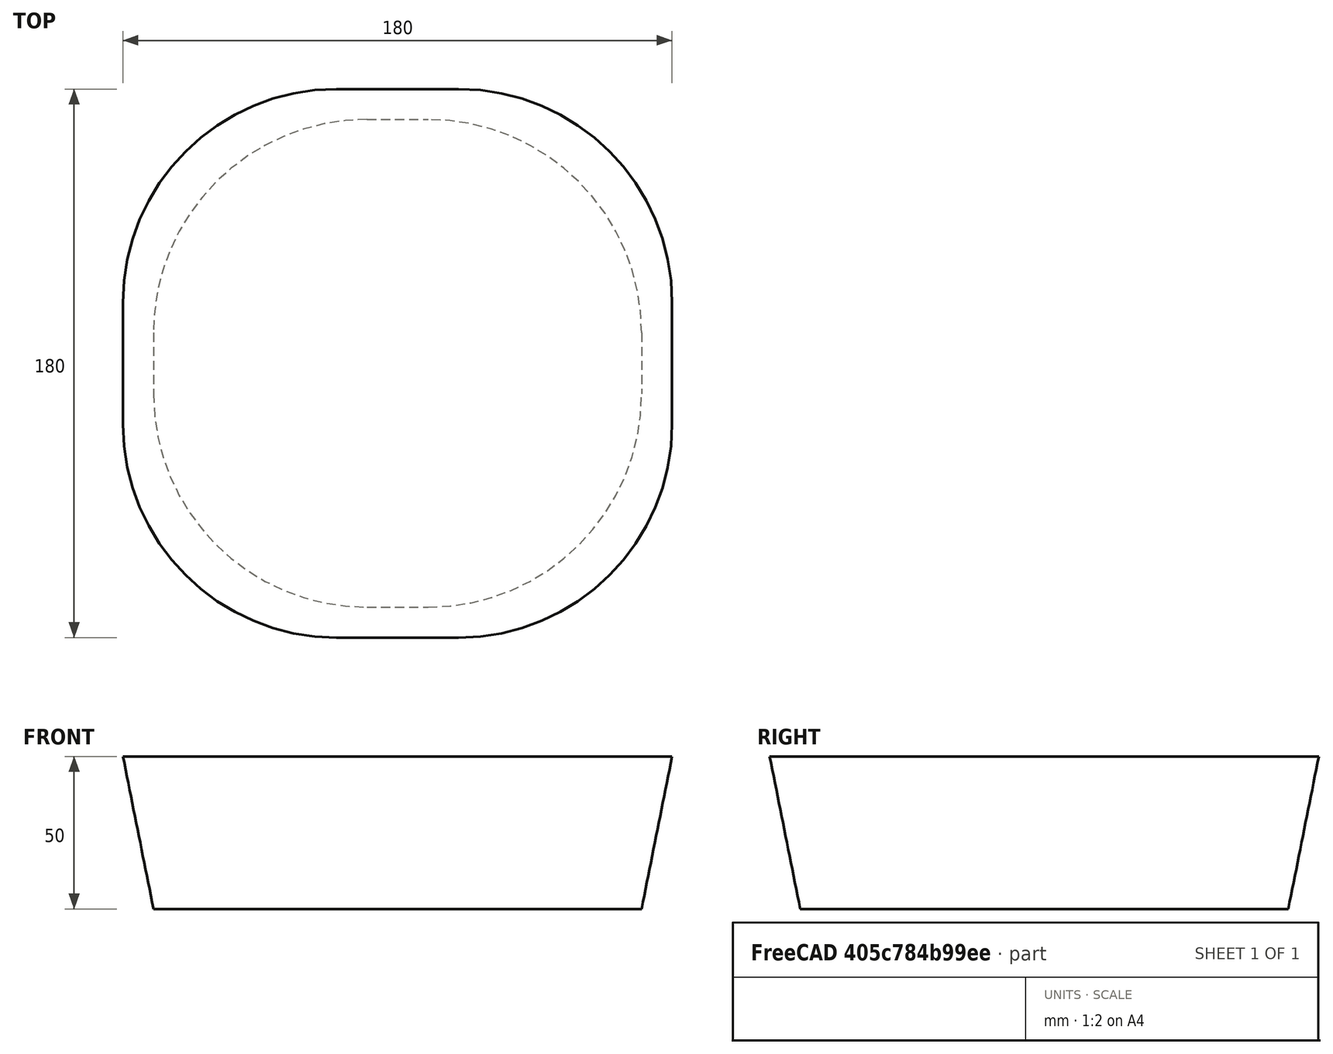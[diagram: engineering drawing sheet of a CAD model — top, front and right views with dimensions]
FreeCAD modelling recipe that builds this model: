
FCSTD DOCUMENT  (FreeCAD 1.1RUnknown)
Label: FlowerPotBowl
License: All rights reserved
LicenseURL: https://en.wikipedia.org/wiki/All_rights_reserved
objects: Sketcher::SketchObject×2, Part::Face×2, App::Point×1, PartDesign::Body×1, Part::Loft×1
note: 8 computed .brp shape members not serialized (recipe doc carries the construction recipe); baked Part::Feature solids carry a one-line shape summary decoded from their .brp

FEATURE [App::Point] Origin001
  Role = Origin
FEATURE [Sketcher::SketchObject] Sketch
  ArcFitTolerance = 1e-06
  AttachmentSupport = -> [Origin]
  ExternalTypes = [0]
  FullyConstrained = true
  MakeInternals = false
  MapMode = 5
  _ExternalGeoVersion = 1
  sketch-geometry (8):
    g0: ArcOfCircle CenterX=70 CenterY=70 CenterZ=0 NormalX=0 NormalY=0 NormalZ=1 AngleXU=0 Radius=70 StartAngle=3.14159 EndAngle=4.71239
    g1: ArcOfCircle CenterX=90 CenterY=70 CenterZ=0 NormalX=0 NormalY=0 NormalZ=1 AngleXU=0 Radius=70 StartAngle=4.71239 EndAngle=6.28319
    g2: ArcOfCircle CenterX=90 CenterY=90 CenterZ=0 NormalX=0 NormalY=0 NormalZ=1 AngleXU=0 Radius=70 StartAngle=0 EndAngle=1.5708
    g3: ArcOfCircle CenterX=70 CenterY=90 CenterZ=0 NormalX=0 NormalY=0 NormalZ=1 AngleXU=0 Radius=70 StartAngle=1.5708 EndAngle=3.14159
    g4: LineSegment StartX=70 StartY=160 StartZ=0 EndX=90 EndY=160 EndZ=0
    g5: LineSegment StartX=160 StartY=90 StartZ=0 EndX=160 EndY=70 EndZ=0
    g6: LineSegment StartX=70 StartY=0 StartZ=0 EndX=90 EndY=0 EndZ=0
    g7: LineSegment StartX=-1.42e-14 StartY=90 StartZ=0 EndX=-1.42e-14 EndY=70 EndZ=0
  constraints (29):
    c: Coincident(g4,g3)
    c: Coincident(g4,g2)
    c: Coincident(g5,g2)
    c: Coincident(g5,g1)
    c: Coincident(g6,g0)
    c: Coincident(g6,g1)
    c: Coincident(g7,g0)
    c: Vertical(g7)
    c: Horizontal(g4)
    c: Horizontal(g6)
    c: Vertical(g5)
    c: Horizontal(g3,g7)
    c: Horizontal(g7,g3)
    c: Horizontal(g3,g2)
    c: Horizontal(g2,g2)
    c: Vertical(g4,g3)
    c: Vertical(g3,g0)
    c: Vertical(g0,g0)
    c: Vertical(g4,g2)
    c: Vertical(g2,g1)
    c: Vertical(g1,g1)
    c: Horizontal(g5,g1)
    c: Horizontal(g1,g0)
    c: Horizontal(g0,g0)
    c: Radius(g0) = 70
    c: Horizontal(g0,g-1)
    c: Vertical(g7,g-1)
    c: DistanceX(g0,g1) = 160
    c: DistanceY(g0,g3) = 160
FEATURE [PartDesign::Body] Body
  AllowCompound = true
  Group = -> [Sketch]
  Origin = -> Origin
FEATURE [Part::Face] Face
  FaceMakerClass = Part::FaceMakerBullseye
  Sources = -> [Sketch]
FEATURE [Sketcher::SketchObject] Sketch001
  ArcFitTolerance = 1e-06
  AttachmentSupport = -> [Sketch]
  ExternalGeometry = -> [Sketch]
  ExternalTypes = [0,0]
  FullyConstrained = true
  MakeInternals = false
  MapMode = 2
  _ExternalGeoVersion = 1
  sketch-geometry (13):
    g0: LineSegment [constr] StartX=-1.42e-14 StartY=90 StartZ=0 EndX=160 EndY=70 EndZ=0
    g1: LineSegment [constr] StartX=160 StartY=90 StartZ=0 EndX=0 EndY=70 EndZ=0
    g2: GeomPoint [constr] X=80 Y=80 Z=0
    g3: ArcOfCircle CenterX=60 CenterY=60 CenterZ=0 NormalX=0 NormalY=0 NormalZ=1 AngleXU=0 Radius=70 StartAngle=3.14159 EndAngle=4.71239
    g4: ArcOfCircle CenterX=100 CenterY=60 CenterZ=0 NormalX=0 NormalY=0 NormalZ=1 AngleXU=0 Radius=70 StartAngle=4.71239 EndAngle=6.28319
    g5: ArcOfCircle CenterX=100 CenterY=100 CenterZ=0 NormalX=0 NormalY=0 NormalZ=1 AngleXU=0 Radius=70 StartAngle=0 EndAngle=1.5708
    g6: ArcOfCircle CenterX=60 CenterY=100 CenterZ=0 NormalX=0 NormalY=0 NormalZ=1 AngleXU=0 Radius=70 StartAngle=1.5708 EndAngle=3.14159
    g7: LineSegment StartX=100 StartY=170 StartZ=0 EndX=60 EndY=170 EndZ=0
    g8: LineSegment StartX=-10 StartY=100 StartZ=0 EndX=-10 EndY=60 EndZ=0
    g9: LineSegment StartX=60 StartY=-10 StartZ=0 EndX=100 EndY=-10 EndZ=0
    g10: LineSegment StartX=170 StartY=60 StartZ=0 EndX=170 EndY=100 EndZ=0
    g11: LineSegment [constr] StartX=60 StartY=170 StartZ=0 EndX=100 EndY=-10 EndZ=0
    g12: LineSegment [constr] StartX=60 StartY=-10 StartZ=0 EndX=100 EndY=170 EndZ=0
  constraints (38):
    c: Coincident(g0,g-4)
    c: Coincident(g0,g-3)
    c: Coincident(g1,g-3)
    c: Coincident(g1,g-4)
    c: PointOnObject(g2,g0)
    c: PointOnObject(g2,g1)
    c: Coincident(g7,g5)
    c: Coincident(g7,g6)
    c: Coincident(g8,g6)
    c: Coincident(g8,g3)
    c: Coincident(g9,g3)
    c: Coincident(g9,g4)
    c: Horizontal(g9)
    c: Coincident(g10,g4)
    c: Coincident(g10,g5)
    c: Vertical(g10)
    c: Vertical(g8)
    c: Horizontal(g7)
    c: Horizontal(g8,g3)
    c: Horizontal(g3,g4)
    c: Horizontal(g4,g4)
    c: Horizontal(g8,g6)
    c: Horizontal(g6,g5)
    c: Horizontal(g5,g5)
    c: Vertical(g7,g6)
    c: Vertical(g6,g3)
    c: Vertical(g3,g3)
    c: Vertical(g7,g5)
    c: Vertical(g4,g4)
    c: Radius(g3) = 70
    c: DistanceX(g3,g4) = 180
    c: DistanceY(g3,g6) = 180
    c: Coincident(g11,g6)
    c: Coincident(g11,g4)
    c: Coincident(g12,g3)
    c: Coincident(g12,g5)
    c: PointOnObject(g2,g11)
    c: PointOnObject(g2,g12)
FEATURE [Part::Face] Face001
  FaceMakerClass = Part::FaceMakerBullseye
  Placement = pos=(0,0,50) rot=(0,0,1;0rad)
  Sources = -> [Sketch001]
FEATURE [Part::Loft] Loft
  Closed = false
  MaxDegree = 5
  Ruled = false
  Sections = -> [Face,Face001]
  Solid = true
